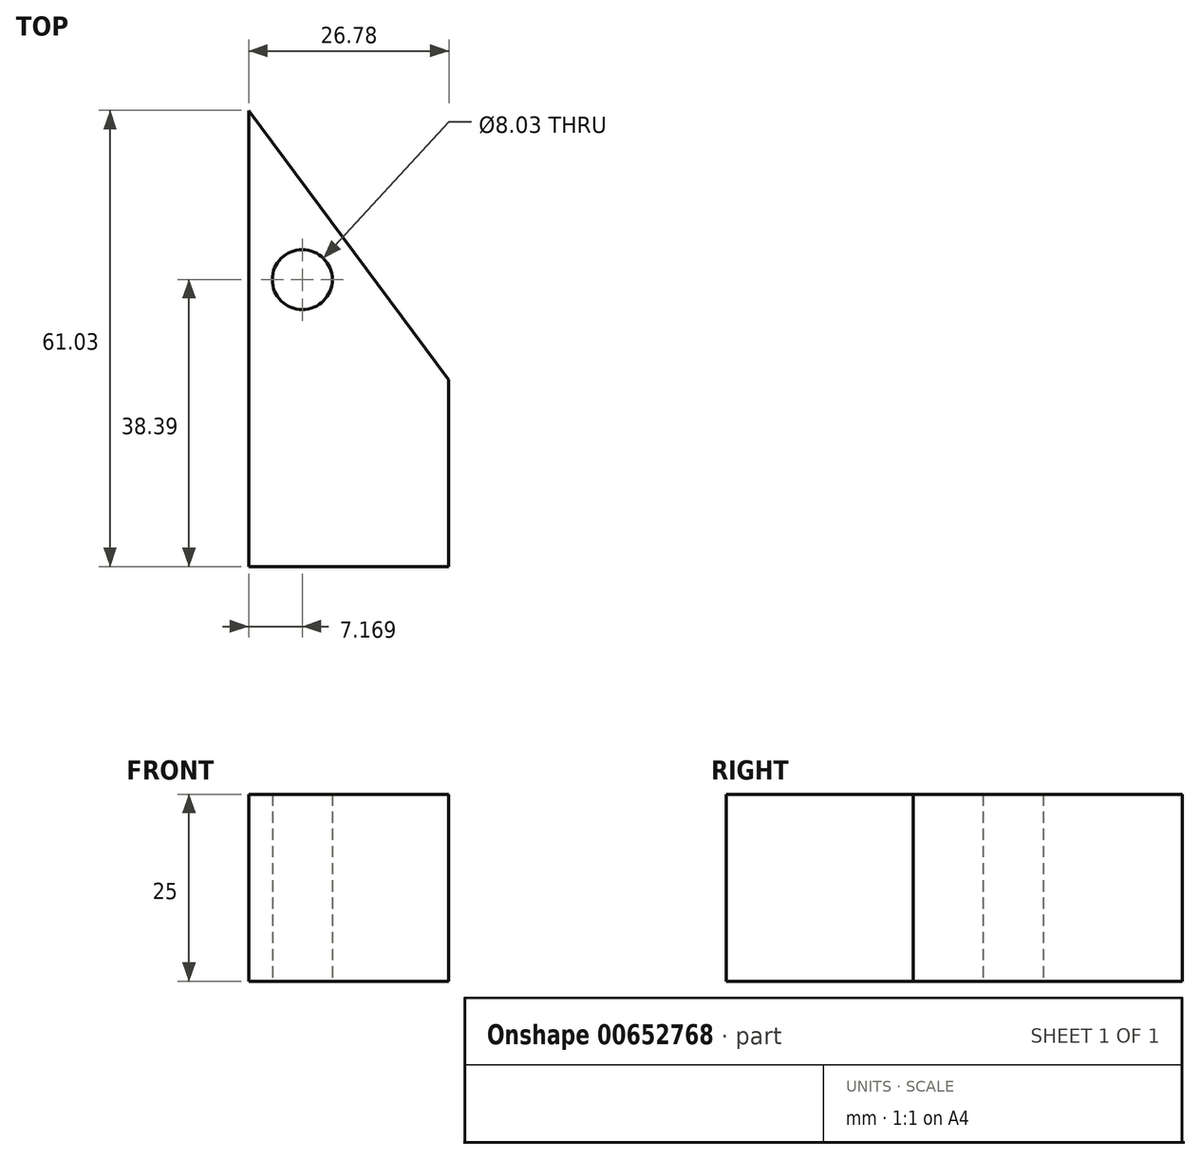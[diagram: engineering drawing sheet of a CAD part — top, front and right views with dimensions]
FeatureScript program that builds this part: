
annotation { "Feature Type Name" : "Feature", "Feature Type Description" : "" }
export const myFeature = defineFeature(function(context is Context, id is Id, definition is map)
    precondition{}
    {
        {
            var Q0;
            Q0=qCreatedBy(makeId("Top.planeOp"),FACE);
            var sketch = newSketch(context, id + "F0", { "sketchPlane" : qUnion([Q0])});
            skLineSegment(sketch, "E0", {"start": v(-58.42, 44.4) * mm, "end": v(-58.42, 8.37) * mm});
            skLineSegment(sketch, "E1", {"start": v(-58.42, 8.37) * mm, "end": v(-31.64, 8.37) * mm});
            skLineSegment(sketch, "E2", {"start": v(-31.64, 8.37) * mm, "end": v(-58.42, 44.4) * mm});
            skSolve(sketch);
        }
        {
            var Q0;
            Q0 = qSketchRegion(id + "F0", true);
            extrude(context, id + "F1", {"entities" : qUnion([Q0]), "depth" : 25 * mm, "offsetDistance" : 25 * mm});
        }
        {
            var Q0;
            Q0=makeQuery(id+"F1.opExtrude","SWEPT_FACE",FACE,{"disambiguationData":[OSD([sQuery(id+"F0.wireOp",EDGE,"E1")])]});
            extrude(context, id + "F2", {"entities" : qUnion([Q0]), "operationType" : NewBodyOperationType.ADD, "depth" : 25 * mm, "offsetDistance" : 25 * mm});
        }
        {
            var Q0;
            {var subQ0=sQuery(id+"F0.wireOp",EDGE,"E1");Q0=makeQuery(id+"F2.boolean.opBoolean","MERGE",FACE,{"derivedFrom":[makeQuery(id+"F1.opExtrude","CAP_FACE",FACE,{"disambiguationData":[OSD([sQuery(id+"F0.wireOp",EDGE,"E0"),subQ0,sQuery(id+"F0.wireOp",EDGE,"E2")])],"isStart":true}),makeQuery(id+"F2.opExtrude","SWEPT_FACE",FACE,{"disambiguationData":[OSD([subQ0]),TDD([makeQuery(id+"F1.opExtrude","CAP_EDGE",EDGE,{"disambiguationData":[OSD([subQ0])],"isStart":true})])]})]});}
            var sketch = newSketch(context, id + "F3", { "sketchPlane" : qUnion([Q0])});
            skCircle(sketch, "E3", {"center": v(-51.25, -21.76) * mm, "radius": 4.01 * mm});
            skSolve(sketch);
        }
        {
            var Q0;
            Q0 = qSketchRegion(id + "F3", true);
            extrude(context, id + "F4", {"entities" : qUnion([Q0]), "operationType" : NewBodyOperationType.REMOVE, "endBound" : BoundingType.THROUGH_ALL, "oppositeDirection" : true, "depth" : 25 * mm, "offsetDistance" : 25 * mm});
        }
    });
